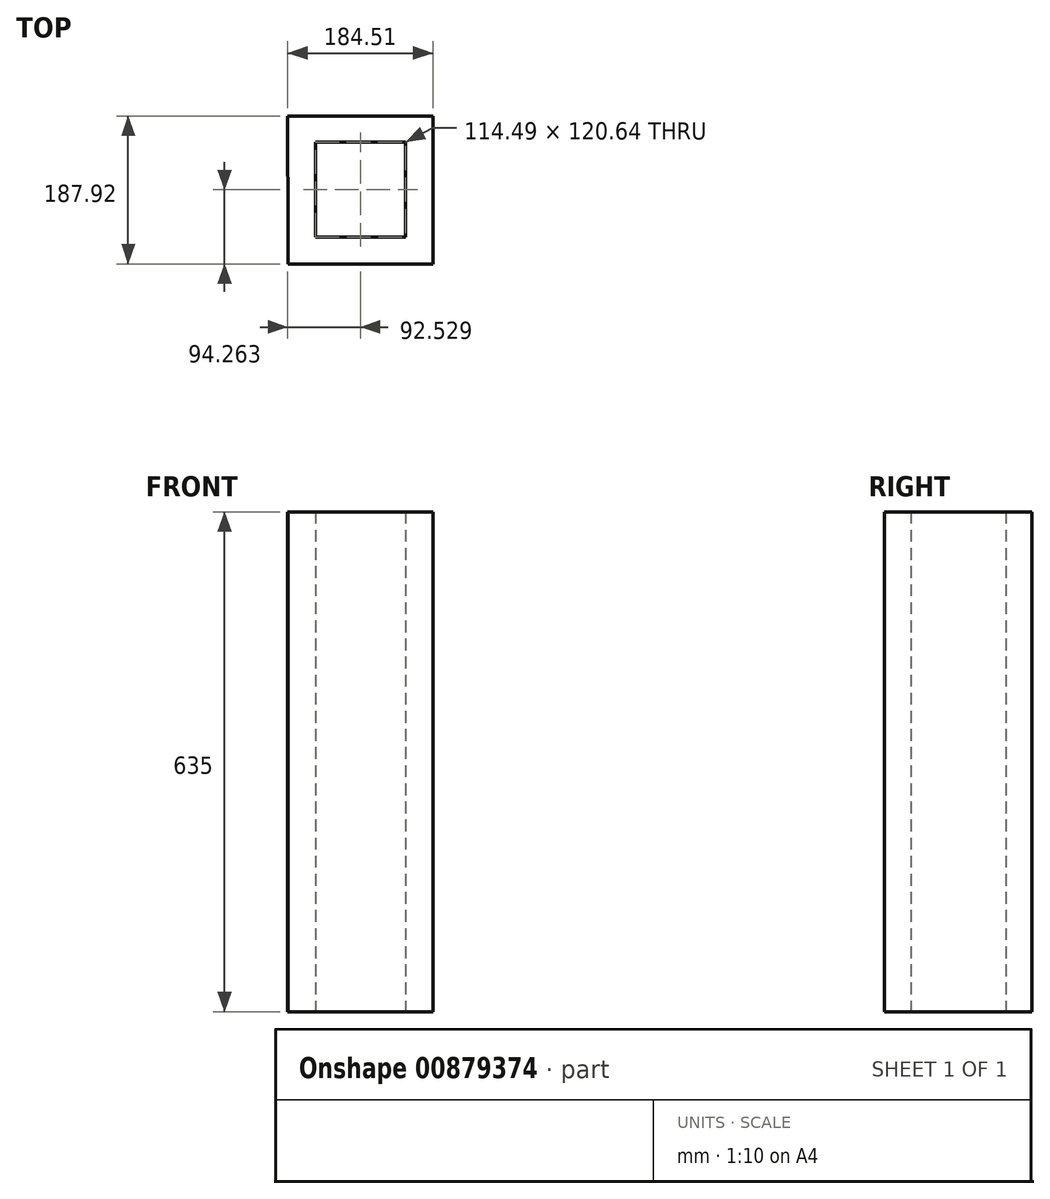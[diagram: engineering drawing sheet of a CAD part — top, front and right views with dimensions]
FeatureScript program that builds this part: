
annotation { "Feature Type Name" : "Feature", "Feature Type Description" : "" }
export const myFeature = defineFeature(function(context is Context, id is Id, definition is map)
    precondition{}
    {
        {
            var Q0;
            Q0=qCreatedBy(makeId("Top.planeOp"),FACE);
            var sketch = newSketch(context, id + "F0", { "sketchPlane" : qUnion([Q0])});
            skLineSegment(sketch, "E0", {"start": v(-92.03, 92.21) * mm, "end": v(92.48, 92.21) * mm});
            skLineSegment(sketch, "E1", {"start": v(92.48, 92.21) * mm, "end": v(92.48, -95.7) * mm});
            skLineSegment(sketch, "E2", {"start": v(92.48, -95.7) * mm, "end": v(-91.25, -95.7) * mm});
            skLineSegment(sketch, "E3", {"start": v(-91.25, -95.7) * mm, "end": v(-92.03, 92.21) * mm});
            skLineSegment(sketch, "E4.top", {"start": v(-92.03, 58.87) * mm, "end": v(-91.89, 58.87) * mm});
            skLineSegment(sketch, "E4.left", {"start": v(-92.03, 92.21) * mm, "end": v(-92.03, 58.87) * mm});
            skLineSegment(sketch, "E4.right", {"start": v(92.48, 92.21) * mm, "end": v(92.48, 58.87) * mm});
            skLineSegment(sketch, "E5.bottom", {"start": v(-91.25, -95.7) * mm, "end": v(92.48, -95.7) * mm});
            skLineSegment(sketch, "E5.top", {"start": v(-56.74, -61.77) * mm, "end": v(57.74, -61.77) * mm});
            skLineSegment(sketch, "E5.left", {"start": v(-91.25, -95.7) * mm, "end": v(-91.25, -61.77) * mm});
            skLineSegment(sketch, "E5.right", {"start": v(92.48, -95.7) * mm, "end": v(92.48, -61.77) * mm});
            skLineSegment(sketch, "E6.bottom", {"start": v(-92.03, 92.21) * mm, "end": v(-56.74, 92.21) * mm});
            skLineSegment(sketch, "E6.top", {"start": v(-92.03, -61.77) * mm, "end": v(-91.25, -61.77) * mm});
            skLineSegment(sketch, "E6.left", {"start": v(-92.03, 92.21) * mm, "end": v(-92.03, -61.77) * mm});
            skLineSegment(sketch, "E6.right", {"start": v(-56.74, 58.87) * mm, "end": v(-56.74, -61.77) * mm});
            skLineSegment(sketch, "E7.left", {"start": v(92.48, 58.87) * mm, "end": v(92.48, -61.77) * mm});
            skLineSegment(sketch, "E7.right", {"start": v(57.74, 58.87) * mm, "end": v(57.74, -61.77) * mm});
            skLineSegment(sketch, "E8.trimOffspring", {"start": v(-56.74, 58.87) * mm, "end": v(57.74, 58.87) * mm});
            skSolve(sketch);
        }
        {
            var Q0;
            Q0=makeQuery(id+"F0.imprint","IMPRINT",FACE,{"disambiguationData":[TD([[makeQuery(id+"F0.imprint","IMPRINT",EDGE,{"derivedFrom":sQuery(id+"F0.wireOp",EDGE,"E0")}),-1.0]])]});
            extrude(context, id + "F1", {"entities" : qUnion([Q0]), "depth" : 635 * mm, "offsetDistance" : 25.4 * mm});
        }
    });
